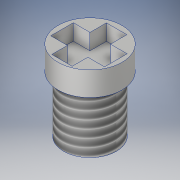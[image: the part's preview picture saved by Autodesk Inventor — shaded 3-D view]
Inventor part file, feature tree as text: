
AUTODESK INVENTOR PART (.ipt)
format: ipt  version: 2018 (Build 220112000, 112)  size: 134,656 bytes
history: native  units: in
note: dims shown in document units (in); Inventor stores cm internally (conversion verified against a paired STEP export)
features: sketch x2, revolve x1, thread x1, extrude x1
ambient origin geometry x8: Origin, YZ Plane, XZ Plane, XY Plane, X Axis, Y Axis, Z Axis, Center Point
bodies: Solid1 (feature_tree)
feature tree (5):
  revolve  "Revolution1"  [1 undecoded]
  thread  "Thread1"  [1 undecoded]
  extrude  "Extrusion1"  TaperAngle=90.0deg  [1 undecoded]
  sketch  "Sketch1"  dims[d0=0.1in d1=0.075in d2=0.0175in]
  sketch  "Sketch2"  dims[d3=0.175in d4=90.0deg d5=1.0in d6=0.0in d7=0.05in d8=0.0in]
note: 3 required parameter values undecoded (feature->parameter linkage not recoverable at this tier; creation-order binding heuristic only, values carry confidence <= 0.55)